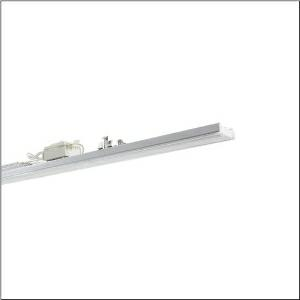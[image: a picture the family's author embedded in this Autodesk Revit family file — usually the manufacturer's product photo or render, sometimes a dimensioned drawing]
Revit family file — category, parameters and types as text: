
# Revit family: licross_11_recessed_mo_51tl18dv48xg
name_source: partatom
category: Lighting Fixtures
units: mm (PartAtom-declared; Revit-internal decimal feet)

## family parameters
Cut with Voids When Loaded = No
Host = Face
Light Source = No
Part Type = Normal
Room Calculation Point = No
Round Connector Dimension = Use Diameter
Shared = No

## types (1)
- --- (1 x LED, 8000 lm, 43.2 W, 4000K)
    Apparent Load = 43 VA
    CIE Flux Codes = 83 96 99 100 100
    Color Rendering = 80
    Color Temperature = 4000K
    Default Elevation = 1800 mm
    Description = Licross 11 Recessed MO, luminaire insert, of sheet steel, coil coated, white, length: 2.250mm, width: 66mm, height: 67mm, LED rated luminous flux: 8.000lm, light colour: 840, SDCM (Standard Deviation of Colour Matching)MacAdam ≤ 2 SDCM (initial), control gear: DALI 2, with plug, 5-pole, with phase selection, mains connection: 220..240V, AC, 50/60Hz, rated input power: 43W, internal wiring halogen-free, primary light control with lens, of plastic, primary optical cover: cover, of PMMA, light emission: direct distribution, primary light characteristic: symmetric, protection rating (complete): IP40, insulation class (complete): insulation class I (protective earthing), certification: CE, ENEC, VDE, UKCA, protection symbol: D if used in an environment without relevant dust loads with corresponding accessories, impact resistance: IK06, permissible ambient temperature for indoor applications: -25..+45°C, corresponds to IFS (International Featured Standards) requirements for safety and quality in the food industry, reducing of maximum allowable ambient temperature of 5°C with ceiling mounting, LABS conformity tested according to VDMA 24364:2018-05, The light source and the operating device comply with the requirements of the Ecodesign Regulation (EU) 2019/2020 and are replaceable in accordance with this regulation, packaging unit: 1 piece
    Height = 58 mm
    Lamp = 1 x LED
    Lamp Light Flux = 8000 lm
    Lamp Power = 43.2 W
    Lamp count = 1
    Length = 2250 mm
    Luminous efficacy = 185 lm/W
    Manufacturer = Siteco
    ModVariant = No
    Model = 51TL18DV48XG
    Mounting Place = Ceiling
    Mounting Type = Pendant
    Number of Poles = 1
    OnlyDefault = Yes
    Power Factor = 1
    Product Name = Licross 11 Recessed MO
    Product group = luminaire insert | ceiling pendant
    ProductGroupID = 901
    Protection Class = Protection class I
    Protection Degree = IP 40
    RLX_Detail_Level = 1
    RLX_Emergency_Light_Flux = 0 lm
    RLX_Emergency_Type = 0
    RLX_Emergency_Type_DB = No
    RlxData = <blob elided: 29209 chars, md5=3a7a98d1>
    Socket = socket
    Standby Power = 0 W
    System Light Flux = 8000 lm
    System Power = 43 W
    Type Comments = factory setting: luminous flux: 100 % | dim-lin: 254 | 194 mA
    Type Image = l_1296930.jpg
    URL = http://relux.com
    VarID = @adj_100695
    Voltage = 0 V
    Weight = 0.00 kg
    Width = 66 mm

## geometry (parser evidence)
native form markers: Blend x4, Sweep x8
no freeform markers — native parametric forms only
